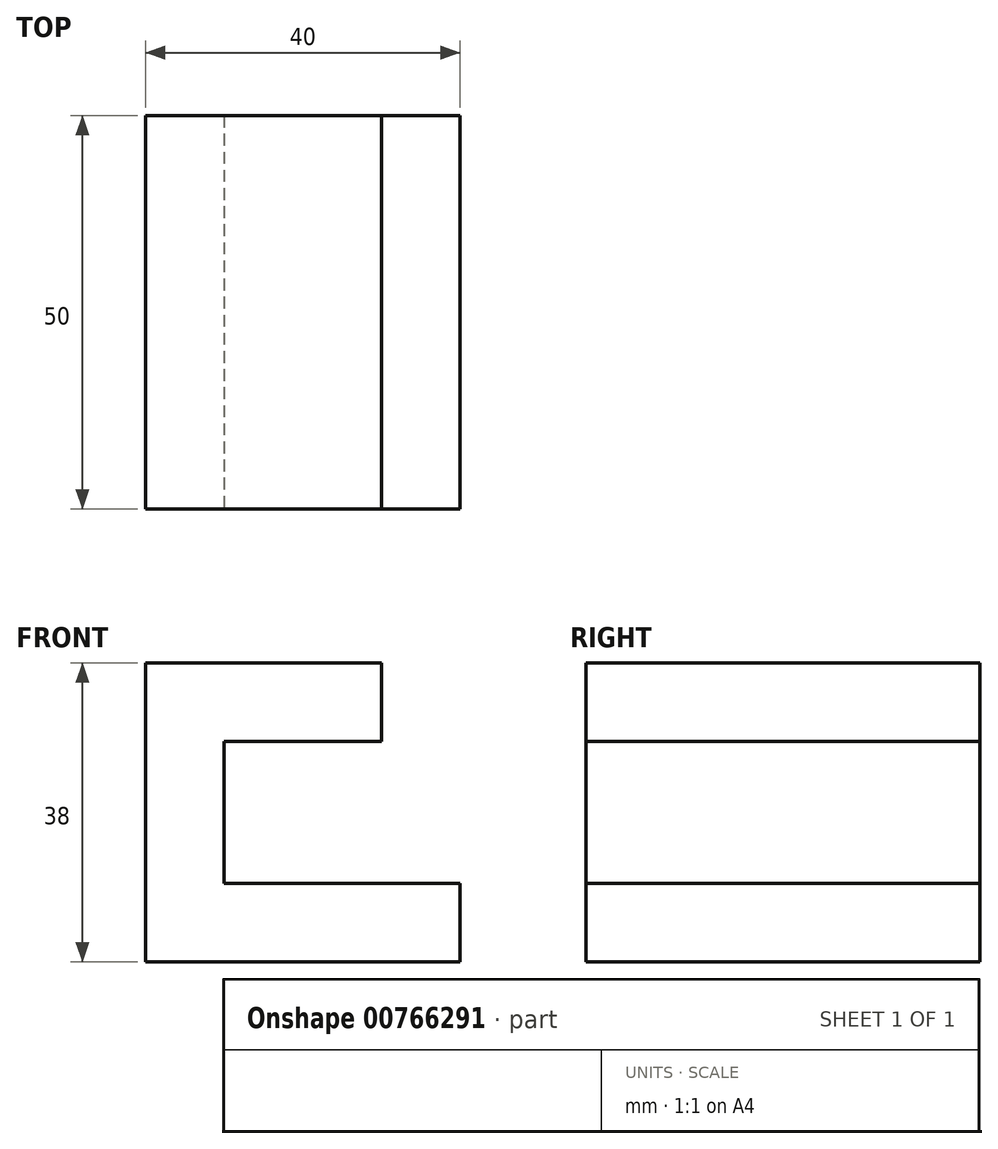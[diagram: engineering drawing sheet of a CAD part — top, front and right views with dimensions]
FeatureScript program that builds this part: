
annotation { "Feature Type Name" : "Feature", "Feature Type Description" : "" }
export const myFeature = defineFeature(function(context is Context, id is Id, definition is map)
    precondition{}
    {
        {
            var Q0;
            Q0=qCreatedBy(makeId("Front.planeOp"),FACE);
            var sketch = newSketch(context, id + "F0", { "sketchPlane" : qUnion([Q0])});
            skLineSegment(sketch, "E0.bottom", {"start": v(15, 38) * mm, "end": v(-15, 38) * mm});
            skLineSegment(sketch, "E0.top", {"start": v(15, 0) * mm, "end": v(-15, 0) * mm});
            skLineSegment(sketch, "E0.left", {"start": v(15, 38) * mm, "end": v(15, 0) * mm});
            skLineSegment(sketch, "E0.right", {"start": v(-15, 38) * mm, "end": v(-15, 0) * mm});
            skLineSegment(sketch, "E1.bottom", {"start": v(-5, 28) * mm, "end": v(15, 28) * mm});
            skLineSegment(sketch, "E1.top", {"start": v(-5, 10) * mm, "end": v(15, 10) * mm});
            skLineSegment(sketch, "E1.left", {"start": v(-5, 28) * mm, "end": v(-5, 10) * mm});
            skLineSegment(sketch, "E1.right", {"start": v(15, 28) * mm, "end": v(15, 10) * mm});
            skLineSegment(sketch, "E2.bottom", {"start": v(15, 10) * mm, "end": v(25, 10) * mm});
            skLineSegment(sketch, "E2.top", {"start": v(15, 0) * mm, "end": v(25, 0) * mm});
            skLineSegment(sketch, "E2.left", {"start": v(15, 10) * mm, "end": v(15, 0) * mm});
            skLineSegment(sketch, "E2.right", {"start": v(25, 10) * mm, "end": v(25, 0) * mm});
            skSolve(sketch);
        }
        {
            var Q0;
            Q0=makeQuery(id+"F0.imprint","IMPRINT",FACE,{"disambiguationData":[TD([[makeQuery(id+"F0.imprint","IMPRINT",EDGE,{"derivedFrom":sQuery(id+"F0.wireOp",EDGE,"E0.bottom")}),1.0]])]});
            var Q1;
            Q1=makeQuery(id+"F0.imprint","IMPRINT",FACE,{"disambiguationData":[TD([[makeQuery(id+"F0.imprint","IMPRINT",EDGE,{"derivedFrom":sQuery(id+"F0.wireOp",EDGE,"E2.bottom")}),-1.0]])]});
            extrude(context, id + "F1", {"entities" : qUnion([Q0, Q1]), "endBound" : BoundingType.SYMMETRIC, "oppositeDirection" : true, "depth" : 50 * mm, "offsetDistance" : 25 * mm});
        }
    });
